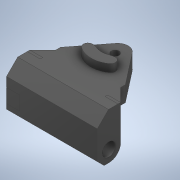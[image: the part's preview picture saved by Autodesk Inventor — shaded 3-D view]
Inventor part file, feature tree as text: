
AUTODESK INVENTOR PART (.ipt)
format: ipt  version: 2020 (Build 240168000, 168)  size: 278,016 bytes
history: native  units: in
note: dims shown in document units (in); Inventor stores cm internally (conversion verified against a paired STEP export)
features: extrude x6, sketch x6, projected_geometry x2, chamfer x1
ambient origin geometry x8: Origin, YZ Plane, XZ Plane, XY Plane, X Axis, Y Axis, Z Axis, Center Point
bodies: Solid2 (feature_tree), Solid1 (feature_tree)
feature tree (15):
  extrude  "add 5mm left side"  Depth=0.1969in TaperAngle=0.0deg
  extrude  "add 5 mm right side"  Depth=0.1969in
  chamfer  "support for 5mm extensions"  Distance=0.1969in
  extrude  "make bean smaller"  TaperAngle=45.0deg  [1 undecoded]
  extrude  "square off round for easy printing"  Depth=0.3937in TaperAngle=0.0deg
  extrude  "make standoff hole bigger"  Depth=0.126in TaperAngle=0.0deg
  extrude  "make bottom plate space bigger"  [1 undecoded]
  sketch  "Sketch1"  dims[d0=0.1969in d1=0.0in d7=0.1969in d8=0.0in]
  sketch  "Sketch2"  dims[d9=0.1969in d10=0.0787in d11=45.0deg d12=0.0039in d13=0.1969in d14=0.0in]
  sketch  "Sketch3"  dims[d15=0.3937in d16=0.0in d18=45.0deg]
  projected_geometry  "Projected Loop1"
  sketch  "Sketch4"  dims[d19=0.2008in d20=0.3937in d21=0.0in]
  projected_geometry  "Projected Loop2"
  sketch  "Sketch5"  dims[d22=0.0118in d23=0.126in d24=0.0in]
  sketch  "Sketch6"
note: 2 required parameter values undecoded (feature->parameter linkage not recoverable at this tier; creation-order binding heuristic only, values carry confidence <= 0.55)
